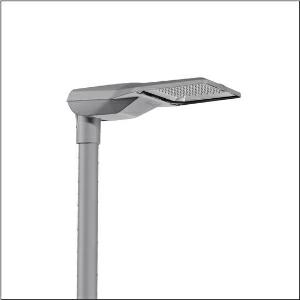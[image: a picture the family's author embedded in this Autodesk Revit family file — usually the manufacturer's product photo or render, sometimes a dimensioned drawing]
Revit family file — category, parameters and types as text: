
# Revit family: streetlight_sl_21_midi___st0_5a_5xe7b43a08lb_42bf
name_source: partatom
category: Lighting Fixtures
units: mm (PartAtom-declared; Revit-internal decimal feet)

## family parameters
Cut with Voids When Loaded = No
Host = Face
Light Source = No
Part Type = Normal
Room Calculation Point = No
Round Connector Dimension = Use Diameter
Shared = No

## types (1)
- --- (1 x LED, 14950 lm, 98.3 W, 4000K)
    Apparent Load = 98 VA
    CIE Flux Codes = 41 75 97 100 100
    Color Rendering = 70
    Color Temperature = 4000K
    Default Elevation = 1800 mm
    Description = Streetlight SL 21 midi, mast luminaire, primary light control with lens, of PMMA, primary optical cover: cover, of toughened safety glass, transparent, light distribution: ST0.5a, light emission: direct distribution, primary light characteristic: asymmetric, installation type: post-top, side-entry, LED, 3G 1.5mm², High Power LED, rated luminous flux: 14.950lm, luminous efficacy: 152lm/W, light colour: 740, colour temperature: 4000K, control: overheat protection, constant luminous flux control, time-dependent luminous flux control, flexible luminous flux parameterisation, mains connection: 220..240V, AC, 50/60Hz, connection cable pre-assembled, cable length: 10,5m, wiring characteristics: H07RN-F, start of lifetime: 98W, end of service life: 101W, reduction: 45W, luminaire housing, of diecast aluminium, powder-coated, Siteco® metallic grey (DB 702S), corrosivity category C5 mid according to DIN EN ISO 12944, please order mast flange separately, inclination adjustable: 0°, 5°, 10°, 15°, sealing non-destructively replaceable, multi-level sealing system, length: 644mm, width: 335mm, height: 110mm, mast flange for spigot size: 42mm (side-entry): 5XC10008XM4, 60/48mm (side-entry/post-top): 5XC10108XM2, 76/60mm (side-entry/post-top): 5XC10108XM1, protection rating (complete): IP66, insulation class (complete): insulation class II (safety insulation), certification: CE, ENEC, ENEC+, VDE, impact resistance: IK09, permissible operating ambient temperature for outdoor applications: -40..+50°C, standard-compliant lighting for roads and squares, packaging unit: 1 piece

Light Distribution: ST0.5a
    Height = 111 mm
    Lamp = 1 x LED
    Lamp Light Flux = 14950 lm
    Lamp Power = 98.3 W
    Lamp count = 1
    Length = 644 mm
    Luminous efficacy = 152 lm/W
    Manufacturer = Siteco
    ModVariant = No
    Model = 5XE7B43A08LB
    Number of Poles = 1
    OnlyDefault = Yes
    Power Factor = 1
    Product Name = Streetlight SL 21 midi | ST0.5a
    Product group = mast luminaire | pylon top
    ProductGroupID = 6100
    Protection Class = Protection class II
    Protection Degree = IP 66
    RLX_Detail_Level = 1
    RLX_Emergency_Light_Flux = 0 lm
    RLX_Emergency_Type = 0
    RLX_Emergency_Type_DB = No
    RlxData = <blob elided: 101673 chars, md5=9a7286c9>
    Socket = socket
    Standby Power = 0 W
    System Light Flux = 14950 lm
    System Power = 98 W
    Type Comments = factory setting: luminous flux: 100 % | Output Level: 100 % | 1020 mA
    Type Image = l_1004298.jpg
    URL = http://relux.com
    VarID = @adj_125671
    Voltage = 0 V
    Weight = 0.00 kg
    Width = 336 mm

## geometry (parser evidence)
native form markers: Blend x4, Sweep x11
no freeform markers — native parametric forms only
